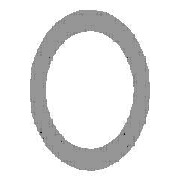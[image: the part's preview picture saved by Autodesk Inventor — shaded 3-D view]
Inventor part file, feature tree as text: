
AUTODESK INVENTOR PART (.ipt)
format: ipt  version: 2013 (Build 170138000, 138)  size: 125,440 bytes
history: native  units: mm (DEFAULTED — no unit token found)
features: plane x7, sketch x5, other x4, extrude x2
ambient origin geometry x8: Origin, YZ Plane, XZ Plane, XY Plane, X Axis, Y Axis, Z Axis, Center Point
bodies: Solid1 (feature_tree), Body (feature_tree)
feature tree (18):
  parser-record x1  (decoder bookkeeping rows leaked as tree rows — omitted from the tree; the rows remain in map.json)
  other  "Driven Length"
  other  "Start plane"
  other  "End plane"
  plane  "Work Plane4"
  plane  "Work Plane5"
  plane  "Work Plane6"
  extrude  "Extrusion2"  Depth=3.556mm
  plane  "Work Plane7"
  plane  "Work Plane8"
  plane  "Work Plane9"
  extrude  "Extrusion3"  TaperAngle=0.0deg  [1 undecoded]
  sketch  "Sketch"  dims[d7=406.4mm d8=3.302mm d9=0.0mm d10=3.302mm d11=0.0mm]
  sketch  "Sketch3"  dims[d0=42.164mm d1=3.556mm]
  plane  "Work Plane3"
  sketch  "Sketch4"  dims[d2=406.4mm d3=0.0mm d4=-0.0mm]
  sketch  "Sketch5"  dims[d5=406.4mm]
  sketch  "Sketch6"  dims[d6=90.0deg]
note: 1 required parameter value undecoded (feature->parameter linkage not recoverable at this tier; creation-order binding heuristic only, values carry confidence <= 0.55)
